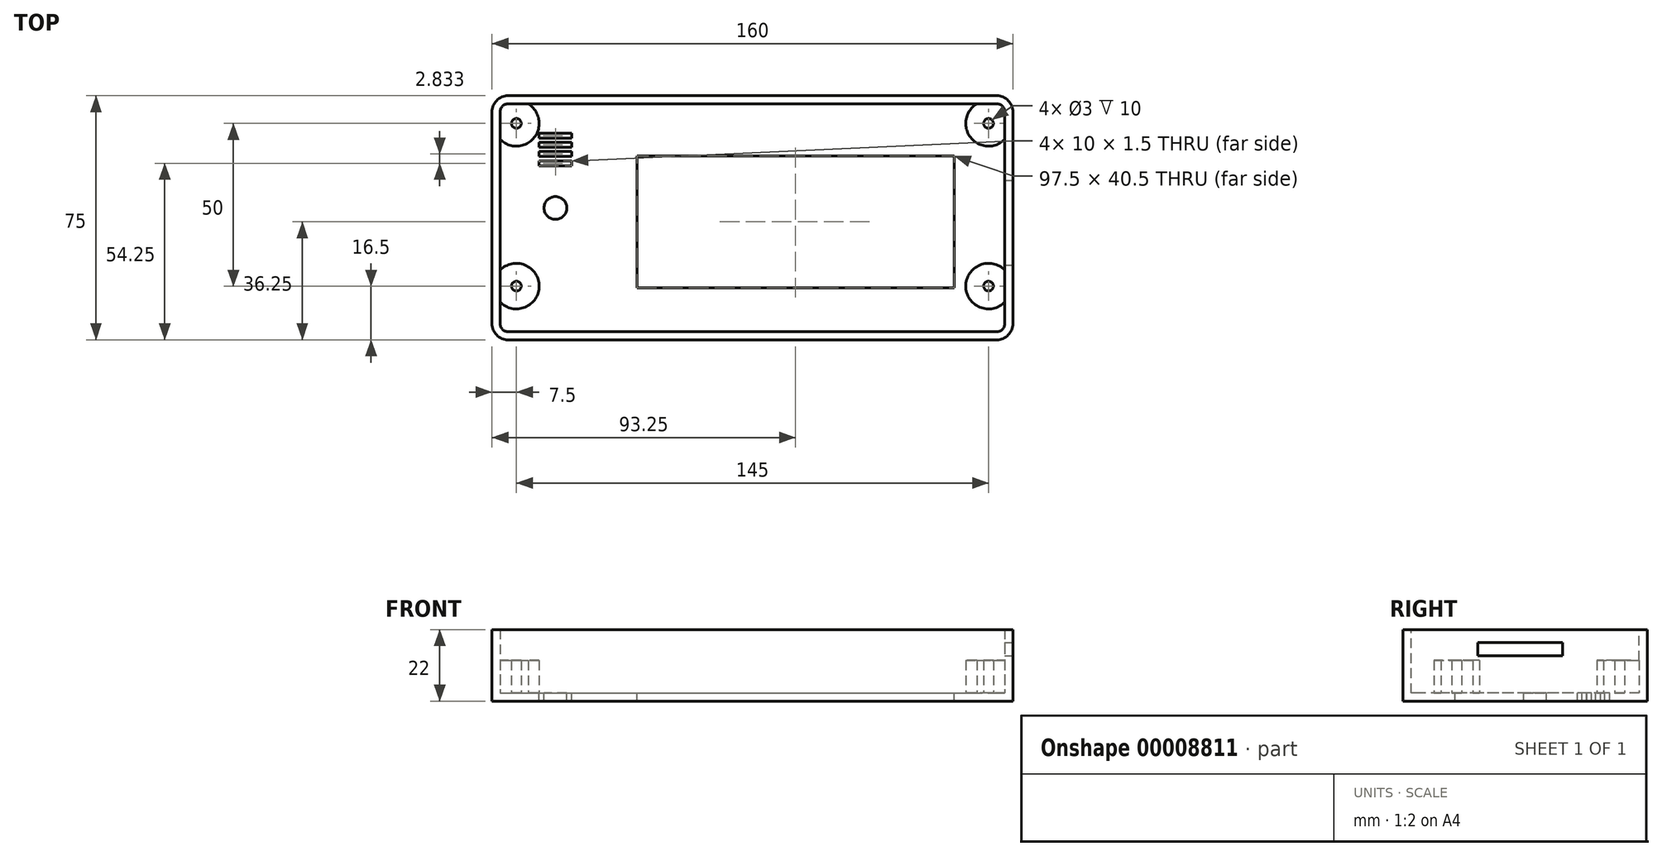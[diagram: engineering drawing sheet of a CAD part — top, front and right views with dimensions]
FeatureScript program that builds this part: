
annotation { "Feature Type Name" : "Feature", "Feature Type Description" : "" }
export const myFeature = defineFeature(function(context is Context, id is Id, definition is map)
    precondition{}
    {
        {
            var Q0;
            Q0=qCreatedBy(makeId("Top.planeOp"),FACE);
            var sketch = newSketch(context, id + "F0", { "sketchPlane" : qUnion([Q0])});
            skLineSegment(sketch, "E0.bottom", {"start": v(-80, 37.5) * mm, "end": v(80, 37.5) * mm});
            skLineSegment(sketch, "E0.top", {"start": v(-80, -37.5) * mm, "end": v(80, -37.5) * mm});
            skLineSegment(sketch, "E0.left", {"start": v(-80, 37.5) * mm, "end": v(-80, -37.5) * mm});
            skLineSegment(sketch, "E0.right", {"start": v(80, 37.5) * mm, "end": v(80, -37.5) * mm});
            skSolve(sketch);
        }
        {
            var Q0;
            Q0=makeQuery(id+"F0.imprint","IMPRINT",FACE,{"disambiguationData":[TD([[makeQuery(id+"F0.imprint","IMPRINT",EDGE,{"derivedFrom":sQuery(id+"F0.wireOp",EDGE,"E0.bottom")}),-1.0]])]});
            extrude(context, id + "F1", {"entities" : qUnion([Q0]), "depth" : 22 * mm});
        }
        {
            var Q0;
            Q0=makeQuery(id+"F1.opExtrude","SWEPT_EDGE",EDGE,{"disambiguationData":[OSD([sQuery(id+"F0.wireOp",EDGE,"E0.top"),sQuery(id+"F0.wireOp",EDGE,"E0.left")])]});
            var Q1;
            Q1=makeQuery(id+"F1.opExtrude","SWEPT_EDGE",EDGE,{"disambiguationData":[OSD([sQuery(id+"F0.wireOp",EDGE,"E0.bottom"),sQuery(id+"F0.wireOp",EDGE,"E0.left")])]});
            var Q2;
            Q2=makeQuery(id+"F1.opExtrude","SWEPT_EDGE",EDGE,{"disambiguationData":[OSD([sQuery(id+"F0.wireOp",EDGE,"E0.bottom"),sQuery(id+"F0.wireOp",EDGE,"E0.right")])]});
            var Q3;
            Q3=makeQuery(id+"F1.opExtrude","SWEPT_EDGE",EDGE,{"disambiguationData":[OSD([sQuery(id+"F0.wireOp",EDGE,"E0.top"),sQuery(id+"F0.wireOp",EDGE,"E0.right")])]});
            fillet(context, id + "F2", {"entities" : qUnion([Q0, Q1, Q2, Q3]), "radius" : 5 * mm, "tangentPropagation" : true, "allowEdgeOverflow" : false});
        }
        {
            var Q0;
            Q0=makeQuery(id+"F1.opExtrude","CAP_FACE",FACE,{"disambiguationData":[OSD([sQuery(id+"F0.wireOp",EDGE,"E0.bottom"),sQuery(id+"F0.wireOp",EDGE,"E0.top"),sQuery(id+"F0.wireOp",EDGE,"E0.left"),sQuery(id+"F0.wireOp",EDGE,"E0.right")])],"isStart":false});
            shell(context, id + "F3", {"entities" : qUnion([Q0]), "thickness" : 2.5 * mm});
        }
        {
            var Q0;
            Q0=makeQuery(id+"F3.opShell","OFFSET_FACE",FACE,{"disambiguationData":[OSD([sQuery(id+"F0.wireOp",EDGE,"E0.bottom"),sQuery(id+"F0.wireOp",EDGE,"E0.top"),sQuery(id+"F0.wireOp",EDGE,"E0.left"),sQuery(id+"F0.wireOp",EDGE,"E0.right")])]});
            var sketch = newSketch(context, id + "F4", { "sketchPlane" : qUnion([Q0])});
            skCircle(sketch, "E1", {"center": v(-72.5, 29) * mm, "radius": 7 * mm});
            skCircle(sketch, "E2", {"center": v(72.5, 29) * mm, "radius": 7 * mm});
            skCircle(sketch, "E3", {"center": v(-72.5, -21) * mm, "radius": 7 * mm});
            skCircle(sketch, "E4", {"center": v(72.5, -21) * mm, "radius": 7 * mm});
            skCircle(sketch, "E5", {"center": v(-72.5, 29) * mm, "radius": 1.5 * mm});
            skCircle(sketch, "E6", {"center": v(-72.5, -21) * mm, "radius": 1.5 * mm});
            skCircle(sketch, "E7", {"center": v(72.5, 29) * mm, "radius": 1.5 * mm});
            skCircle(sketch, "E8", {"center": v(72.5, -21) * mm, "radius": 1.5 * mm});
            skSolve(sketch);
        }
        {
            var Q0;
            Q0=makeQuery(id+"F4.imprint","IMPRINT",FACE,{"disambiguationData":[TD([[makeQuery(id+"F4.imprint","IMPRINT",EDGE,{"derivedFrom":sQuery(id+"F4.wireOp",EDGE,"E1")}),-1.0]])]});
            var sketch = newSketch(context, id + "F5", { "sketchPlane" : qUnion([Q0])});
            skLineSegment(sketch, "E9.bottom", {"start": v(-35.5, 19) * mm, "end": v(62, 19) * mm});
            skLineSegment(sketch, "E9.top", {"start": v(-35.5, -21.5) * mm, "end": v(62, -21.5) * mm});
            skLineSegment(sketch, "E9.left", {"start": v(-35.5, 19) * mm, "end": v(-35.5, -21.5) * mm});
            skLineSegment(sketch, "E9.right", {"start": v(62, 19) * mm, "end": v(62, -21.5) * mm});
            skCircle(sketch, "E10", {"center": v(-60.5, 3) * mm, "radius": 3.5 * mm});
            skLineSegment(sketch, "E11.bottom", {"start": v(-65.5, 23.17) * mm, "end": v(-55.5, 23.17) * mm});
            skLineSegment(sketch, "E11.top", {"start": v(-65.5, 21.67) * mm, "end": v(-55.5, 21.67) * mm});
            skLineSegment(sketch, "E11.left", {"start": v(-65.5, 23.17) * mm, "end": v(-65.5, 21.67) * mm});
            skLineSegment(sketch, "E11.right", {"start": v(-55.5, 23.17) * mm, "end": v(-55.5, 21.67) * mm});
            skLineSegment(sketch, "E12.bottom", {"start": v(-55.5, 20.33) * mm, "end": v(-65.5, 20.33) * mm});
            skLineSegment(sketch, "E12.top", {"start": v(-55.5, 18.83) * mm, "end": v(-65.5, 18.83) * mm});
            skLineSegment(sketch, "E12.left", {"start": v(-55.5, 20.33) * mm, "end": v(-55.5, 18.83) * mm});
            skLineSegment(sketch, "E12.right", {"start": v(-65.5, 20.33) * mm, "end": v(-65.5, 18.83) * mm});
            skLineSegment(sketch, "E13.bottom", {"start": v(-65.5, 17.5) * mm, "end": v(-55.5, 17.5) * mm});
            skLineSegment(sketch, "E13.top", {"start": v(-65.5, 16) * mm, "end": v(-55.5, 16) * mm});
            skLineSegment(sketch, "E13.left", {"start": v(-65.5, 17.5) * mm, "end": v(-65.5, 16) * mm});
            skLineSegment(sketch, "E13.right", {"start": v(-55.5, 17.5) * mm, "end": v(-55.5, 16) * mm});
            skLineSegment(sketch, "E14.bottom", {"start": v(-65.5, 26) * mm, "end": v(-55.5, 26) * mm});
            skLineSegment(sketch, "E14.top", {"start": v(-65.5, 24.5) * mm, "end": v(-55.5, 24.5) * mm});
            skLineSegment(sketch, "E14.left", {"start": v(-65.5, 26) * mm, "end": v(-65.5, 24.5) * mm});
            skLineSegment(sketch, "E14.right", {"start": v(-55.5, 26) * mm, "end": v(-55.5, 24.5) * mm});
            skLineSegment(sketch, "E15", {"start": v(-55.5, 24.5) * mm, "end": v(-55.5, 23.17) * mm, "construction": true});
            skLineSegment(sketch, "E16", {"start": v(-55.5, 21.67) * mm, "end": v(-55.5, 20.33) * mm, "construction": true});
            skLineSegment(sketch, "E17", {"start": v(-55.5, 18.83) * mm, "end": v(-55.5, 17.5) * mm, "construction": true});
            skPoint(sketch, "E18", {"position": v(-60.5, 16) * mm});
            skSolve(sketch);
        }
        {
            var Q0;
            Q0 = qSketchRegion(id + "F5", true);
            extrude(context, id + "F6", {"entities" : qUnion([Q0]), "operationType" : NewBodyOperationType.REMOVE, "oppositeDirection" : true, "depth" : 25 * mm});
        }
        {
            var Q0;
            Q0 = qSketchRegion(id + "F4", true);
            extrude(context, id + "F7", {"entities" : qUnion([Q0]), "operationType" : NewBodyOperationType.ADD, "depth" : 10 * mm});
        }
        {
            var Q0;
            Q0=makeQuery(id+"F1.opExtrude","SWEPT_FACE",FACE,{"disambiguationData":[OSD([sQuery(id+"F0.wireOp",EDGE,"E0.right")])]});
            var sketch = newSketch(context, id + "F8", { "sketchPlane" : qUnion([Q0])});
            skLineSegment(sketch, "E19.bottom", {"start": v(-14.5, 18) * mm, "end": v(11.5, 18) * mm});
            skLineSegment(sketch, "E19.top", {"start": v(-14.5, 14) * mm, "end": v(11.5, 14) * mm});
            skLineSegment(sketch, "E19.left", {"start": v(-14.5, 18) * mm, "end": v(-14.5, 14) * mm});
            skLineSegment(sketch, "E19.right", {"start": v(11.5, 18) * mm, "end": v(11.5, 14) * mm});
            skSolve(sketch);
        }
        {
            var Q0;
            Q0=makeQuery(id+"F8.imprint","IMPRINT",FACE,{"disambiguationData":[TD([[makeQuery(id+"F8.imprint","IMPRINT",EDGE,{"derivedFrom":sQuery(id+"F8.wireOp",EDGE,"E19.bottom")}),-1.0]])]});
            extrude(context, id + "F9", {"entities" : qUnion([Q0]), "operationType" : NewBodyOperationType.REMOVE, "oppositeDirection" : true, "depth" : 25 * mm});
        }
    });
